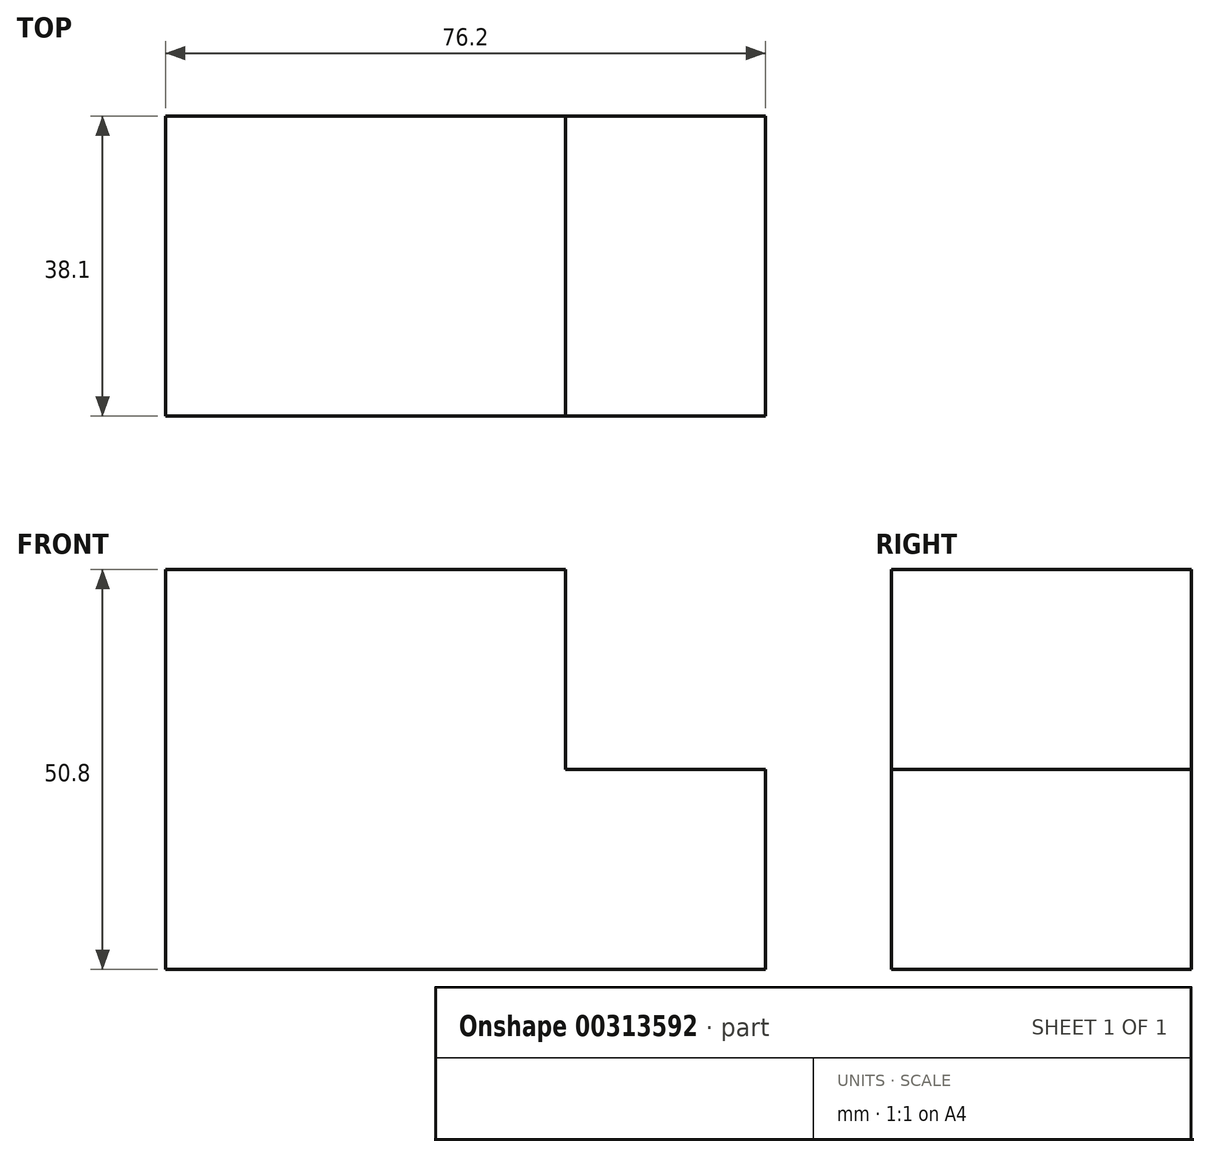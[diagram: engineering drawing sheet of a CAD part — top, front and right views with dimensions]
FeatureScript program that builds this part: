
annotation { "Feature Type Name" : "Feature", "Feature Type Description" : "" }
export const myFeature = defineFeature(function(context is Context, id is Id, definition is map)
    precondition{}
    {
        {
            var Q0;
            Q0=qCreatedBy(makeId("Front.planeOp"),FACE);
            var sketch = newSketch(context, id + "F0", { "sketchPlane" : qUnion([Q0])});
            skLineSegment(sketch, "E0", {"start": v(-38.53, -37.64) * mm, "end": v(37.67, -37.64) * mm});
            skLineSegment(sketch, "E1", {"start": v(37.67, -37.64) * mm, "end": v(37.67, -12.24) * mm});
            skLineSegment(sketch, "E2", {"start": v(37.67, -12.24) * mm, "end": v(12.27, -12.24) * mm});
            skLineSegment(sketch, "E3", {"start": v(12.27, -12.24) * mm, "end": v(12.27, 13.16) * mm});
            skLineSegment(sketch, "E4", {"start": v(12.27, 13.16) * mm, "end": v(-38.53, 13.16) * mm});
            skLineSegment(sketch, "E5", {"start": v(-38.53, 13.16) * mm, "end": v(-38.53, -37.64) * mm});
            skSolve(sketch);
        }
        {
            var Q0;
            Q0=makeQuery(id+"F0.imprint","IMPRINT",FACE,{"disambiguationData":[TD([[makeQuery(id+"F0.imprint","IMPRINT",EDGE,{"derivedFrom":sQuery(id+"F0.wireOp",EDGE,"E0")}),1.0]])]});
            extrude(context, id + "F1", {"entities" : qUnion([Q0]), "depth" : 38.1 * mm});
        }
    });
